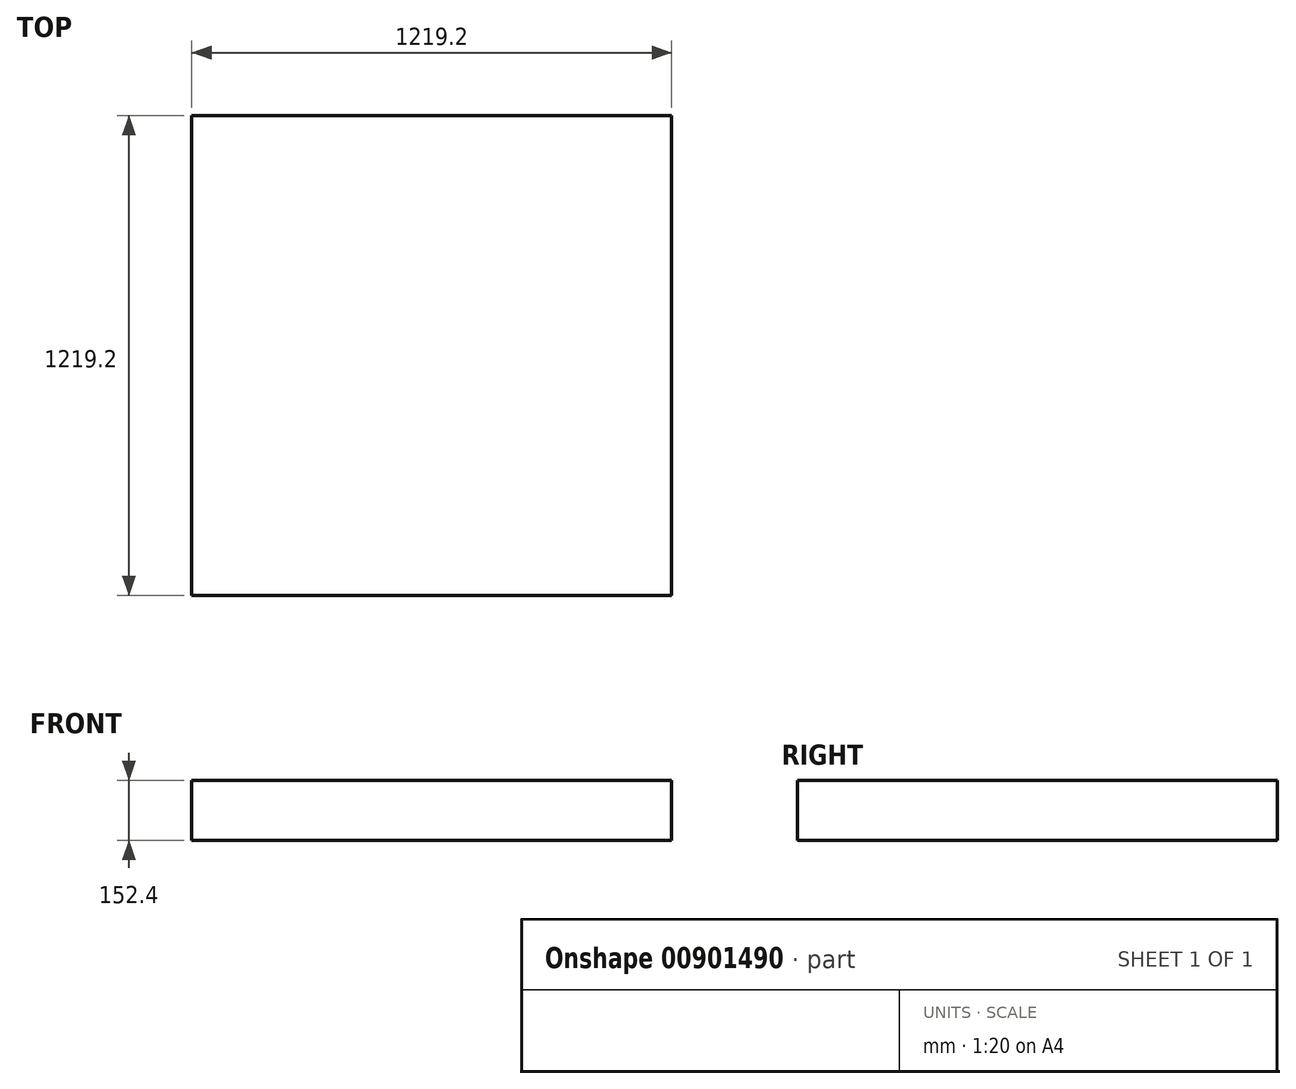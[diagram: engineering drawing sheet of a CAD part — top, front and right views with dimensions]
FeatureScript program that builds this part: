
annotation { "Feature Type Name" : "Feature", "Feature Type Description" : "" }
export const myFeature = defineFeature(function(context is Context, id is Id, definition is map)
    precondition{}
    {
        {
            var Q0;
            Q0=qCreatedBy(makeId("Top.planeOp"),FACE);
            var sketch = newSketch(context, id + "F0", { "sketchPlane" : qUnion([Q0])});
            skLineSegment(sketch, "E0.bottom", {"start": v(609.6, -609.6) * mm, "end": v(-609.6, -609.6) * mm});
            skLineSegment(sketch, "E0.top", {"start": v(609.6, 609.6) * mm, "end": v(-609.6, 609.6) * mm});
            skLineSegment(sketch, "E0.left", {"start": v(609.6, -609.6) * mm, "end": v(609.6, 609.6) * mm});
            skLineSegment(sketch, "E0.right", {"start": v(-609.6, -609.6) * mm, "end": v(-609.6, 609.6) * mm});
            skPoint(sketch, "E0.middle", {"position": v(0, 0) * mm});
            skSolve(sketch);
        }
        {
            var Q0;
            Q0 = qSketchRegion(id + "F0", true);
            extrude(context, id + "F1", {"entities" : qUnion([Q0]), "endBound" : BoundingType.SYMMETRIC, "depth" : 152.4 * mm, "offsetDistance" : 25.4 * mm});
        }
    });
